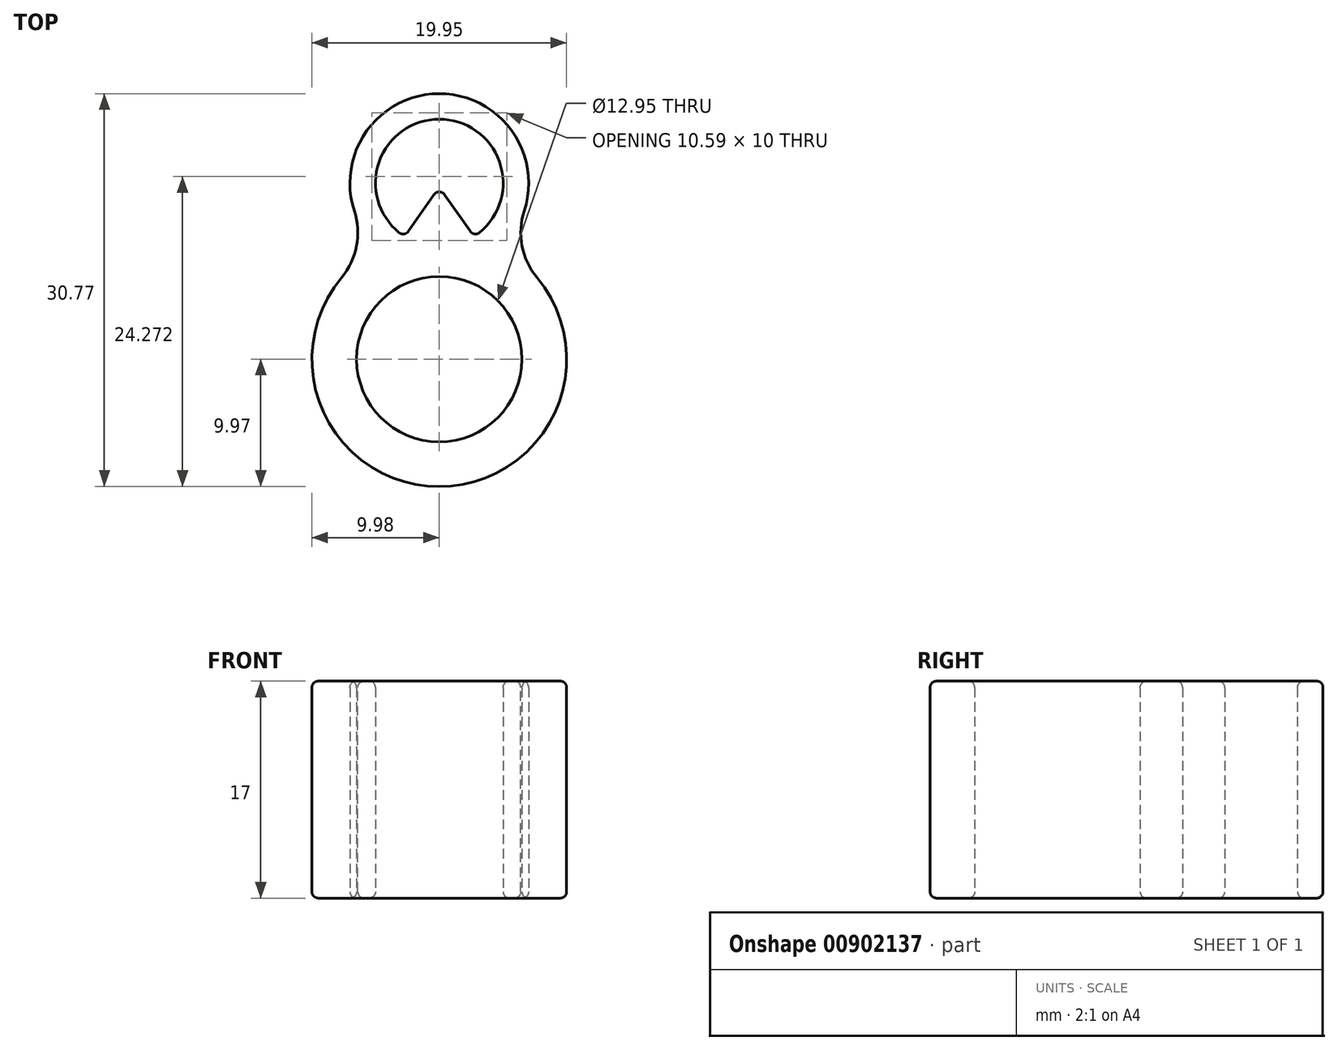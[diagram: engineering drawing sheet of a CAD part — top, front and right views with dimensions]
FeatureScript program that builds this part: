
annotation { "Feature Type Name" : "Feature", "Feature Type Description" : "" }
export const myFeature = defineFeature(function(context is Context, id is Id, definition is map)
    precondition{}
    {
        {
            var Q0;
            Q0=qCreatedBy(makeId("Top.planeOp"),FACE);
            var sketch = newSketch(context, id + "F0", { "sketchPlane" : qUnion([Q0])});
            skCircle(sketch, "E0", {"center": v(0, 0) * mm, "radius": 6.48 * mm});
            skArc(sketch, "E1", {"start": v(-4.83, 8.73) * mm, "mid": v(0, -9.97) * mm, "end": v(4.83, 8.73) * mm});
            skArc(sketch, "E2", {"start": v(3.15, 9.91) * mm, "mid": v(0, 18.8) * mm, "end": v(-3.15, 9.91) * mm});
            skLineSegment(sketch, "E3", {"start": v(-2.42, 10.02) * mm, "end": v(-0.4, 12.89) * mm});
            skLineSegment(sketch, "E4", {"start": v(0.4, 12.89) * mm, "end": v(2.42, 10.02) * mm});
            skPoint(sketch, "E5.visualSharp", {"position": v(0, 13.47) * mm});
            skArc(sketch, "E5.filletArc", {"start": v(0.4, 12.89) * mm, "mid": v(0, 13.1) * mm, "end": v(-0.4, 12.89) * mm});
            skArc(sketch, "E6", {"start": v(4.83, 8.73) * mm, "mid": v(0, 20.8) * mm, "end": v(-4.83, 8.73) * mm});
            skPoint(sketch, "E7.visualSharp", {"position": v(-2.71, 9.6) * mm});
            skArc(sketch, "E7.filletArc", {"start": v(-3.15, 9.91) * mm, "mid": v(-2.76, 9.8) * mm, "end": v(-2.42, 10.02) * mm});
            skPoint(sketch, "E8.visualSharp", {"position": v(2.71, 9.6) * mm});
            skArc(sketch, "E8.filletArc", {"start": v(2.42, 10.02) * mm, "mid": v(2.76, 9.8) * mm, "end": v(3.15, 9.91) * mm});
            skSolve(sketch);
        }
        {
            var Q0;
            Q0=makeQuery(id+"F0.imprint","IMPRINT",FACE,{"disambiguationData":[TD([[makeQuery(id+"F0.imprint","IMPRINT",EDGE,{"derivedFrom":sQuery(id+"F0.wireOp",EDGE,"E0")}),-1.0]])]});
            extrude(context, id + "F1", {"entities" : qUnion([Q0]), "depth" : 17 * mm, "offsetDistance" : 25 * mm});
        }
        {
            var Q0;
            {var subQ0=sQuery(id+"F0.wireOp",EDGE,"E6");var subQ1=sQuery(id+"F0.wireOp",EDGE,"E1");Q0=makeQuery(id+"F1.opExtrude","SWEPT_EDGE",EDGE,{"disambiguationData":[OSD([subQ1,subQ0]),TDD([makeQuery(id+"F0.imprint","INTERSECT",VERTEX,{"disambiguationData":[OD(0.0)],"derivedFrom":[subQ1,subQ0]})])]});}
            var Q1;
            {var subQ0=sQuery(id+"F0.wireOp",EDGE,"E6");var subQ1=sQuery(id+"F0.wireOp",EDGE,"E1");Q1=makeQuery(id+"F1.opExtrude","SWEPT_EDGE",EDGE,{"disambiguationData":[OSD([subQ1,subQ0]),TDD([makeQuery(id+"F0.imprint","INTERSECT",VERTEX,{"disambiguationData":[OD(1.0)],"derivedFrom":[subQ1,subQ0]})])]});}
            fillet(context, id + "F2", {"entities" : qUnion([Q0, Q1]), "radius" : 5.5 * mm, "tangentPropagation" : true, "allowEdgeOverflow" : false});
        }
        {
            var Q0;
            Q0=makeQuery(id+"F1.opExtrude","CAP_EDGE",EDGE,{"disambiguationData":[OSD([sQuery(id+"F0.wireOp",EDGE,"E2")])],"isStart":false});
            var Q1;
            Q1=makeQuery(id+"F1.opExtrude","CAP_EDGE",EDGE,{"disambiguationData":[OSD([sQuery(id+"F0.wireOp",EDGE,"E3")])],"isStart":false});
            var Q2;
            Q2=makeQuery(id+"F1.opExtrude","CAP_EDGE",EDGE,{"disambiguationData":[OSD([sQuery(id+"F0.wireOp",EDGE,"E7.filletArc")])],"isStart":false});
            var Q3;
            Q3=makeQuery(id+"F1.opExtrude","CAP_EDGE",EDGE,{"disambiguationData":[OSD([sQuery(id+"F0.wireOp",EDGE,"E4")])],"isStart":false});
            var Q4;
            Q4=makeQuery(id+"F1.opExtrude","CAP_EDGE",EDGE,{"disambiguationData":[OSD([sQuery(id+"F0.wireOp",EDGE,"E5.filletArc")])],"isStart":false});
            var Q5;
            Q5=makeQuery(id+"F1.opExtrude","CAP_EDGE",EDGE,{"disambiguationData":[OSD([sQuery(id+"F0.wireOp",EDGE,"E8.filletArc")])],"isStart":false});
            var Q6;
            {var subQ0=sQuery(id+"F0.wireOp",EDGE,"E6");var subQ1=sQuery(id+"F0.wireOp",EDGE,"E1");Q6=makeQuery(id+"F2.opFillet","BLEND_EDGE",EDGE,{"blendedFrom":[makeQuery(id+"F1.opExtrude","SWEPT_EDGE",EDGE,{"disambiguationData":[OSD([subQ1,subQ0]),TDD([makeQuery(id+"F0.imprint","INTERSECT",VERTEX,{"disambiguationData":[OD(1.0)],"derivedFrom":[subQ1,subQ0]})])]}),makeQuery(id+"F1.opExtrude","CAP_FACE",FACE,{"disambiguationData":[OSD([sQuery(id+"F0.wireOp",EDGE,"E0"),subQ1,sQuery(id+"F0.wireOp",EDGE,"E2"),sQuery(id+"F0.wireOp",EDGE,"E3"),sQuery(id+"F0.wireOp",EDGE,"E4"),sQuery(id+"F0.wireOp",EDGE,"E5.filletArc"),subQ0,sQuery(id+"F0.wireOp",EDGE,"E7.filletArc"),sQuery(id+"F0.wireOp",EDGE,"E8.filletArc")])],"isStart":false})],"blendedInto":[makeQuery(id+"F1.opExtrude","CAP_FACE",FACE,{"disambiguationData":[OSD([sQuery(id+"F0.wireOp",EDGE,"E0"),subQ1,sQuery(id+"F0.wireOp",EDGE,"E2"),sQuery(id+"F0.wireOp",EDGE,"E3"),sQuery(id+"F0.wireOp",EDGE,"E4"),sQuery(id+"F0.wireOp",EDGE,"E5.filletArc"),subQ0,sQuery(id+"F0.wireOp",EDGE,"E7.filletArc"),sQuery(id+"F0.wireOp",EDGE,"E8.filletArc")])],"isStart":false})]});}
            var Q7;
            Q7=makeQuery(id+"F1.opExtrude","CAP_EDGE",EDGE,{"disambiguationData":[OSD([sQuery(id+"F0.wireOp",EDGE,"E6")])],"isStart":false});
            var Q8;
            Q8=makeQuery(id+"F1.opExtrude","CAP_EDGE",EDGE,{"disambiguationData":[OSD([sQuery(id+"F0.wireOp",EDGE,"E0")])],"isStart":false});
            var Q9;
            Q9=makeQuery(id+"F1.opExtrude","CAP_EDGE",EDGE,{"disambiguationData":[OSD([sQuery(id+"F0.wireOp",EDGE,"E0")])],"isStart":true});
            var Q10;
            Q10=makeQuery(id+"F1.opExtrude","CAP_EDGE",EDGE,{"disambiguationData":[OSD([sQuery(id+"F0.wireOp",EDGE,"E2")])],"isStart":true});
            var Q11;
            Q11=makeQuery(id+"F1.opExtrude","CAP_EDGE",EDGE,{"disambiguationData":[OSD([sQuery(id+"F0.wireOp",EDGE,"E1")])],"isStart":true});
            fillet(context, id + "F3", {"entities" : qUnion([Q0, Q1, Q2, Q3, Q4, Q5, Q6, Q7, Q8, Q9, Q10, Q11]), "radius" : .5 * mm, "tangentPropagation" : true, "allowEdgeOverflow" : false});
        }
    });
